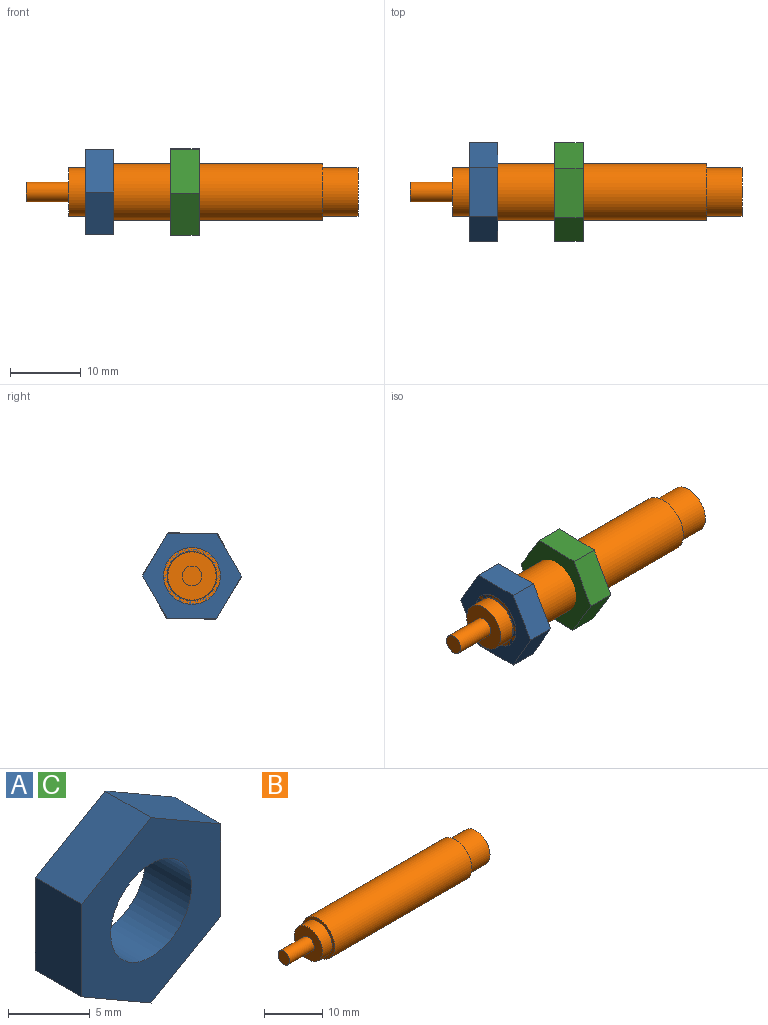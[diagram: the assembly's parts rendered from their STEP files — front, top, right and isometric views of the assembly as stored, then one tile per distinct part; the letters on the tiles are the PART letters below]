
ASSEMBLY  parts=3 mates=4
PART A: 9 faces, bbox 12x4x13.9 mm
  f0: plane 6.02x4mm, normal (0.5,0,0.87), area 27.8mm2, adj f1,f5,f6,f7
  f1: plane 6.02x4mm, normal (-0.5,0,0.87), area 27.8mm2, adj f0,f2,f6,f7
  f2: plane 6.95x4mm, normal (-1,0,0), area 27.8mm2, adj f1,f3,f6,f7
  f3: plane 6.02x4mm, normal (-0.5,0,-0.87), area 27.8mm2, adj f2,f4,f6,f7
  f4: plane 6.02x4mm, normal (0.5,0,-0.87), area 27.8mm2, adj f3,f5,f6,f7
  f5: plane 6.95x4mm, normal (1,0,0), area 27.8mm2, adj f0,f4,f6,f7
  f6: plane 13.9x12.04mm, normal (0,-1,0), area 87mm2, adj f0,f1,f2,f3,f4,f5,f8
  f7: plane 13.9x12.04mm, normal (0,1,0), area 87mm2, adj f0,f1,f2,f3,f4,f5,f8
  f8: cylinder r=3.5mm len=7mm, axis (0,-1,0), area 88mm2, adj f6,f7
PART B: 9 faces, bbox 46.8x8x8 mm
  f0: plane 2.8x2.8mm, normal (-1,0,0), area 6.2mm2, adj f8
  f1: plane 6.8x6.8mm, normal (1,0,0), area 36.3mm2, adj f2
  f2: cylinder r=3.4mm len=6.8mm, axis (1,0,0), area 106.8mm2, adj f1,f3
  f3: plane 8x8mm, normal (1,0,0), area 13.9mm2, adj f2,f4
  f4: cylinder r=4mm len=33.4mm, axis (1,0,0), area 839.4mm2, adj f3,f5
  f5: plane 8x8mm, normal (-1,0,0), area 13.9mm2, adj f4,f6
  f6: cylinder r=3.4mm len=6.8mm, axis (1,0,0), area 51.3mm2, adj f5,f7
  f7: plane 6.8x6.8mm, normal (-1,0,0), area 30.2mm2, adj f6,f8
  f8: cylinder r=1.4mm len=6mm, axis (1,0,0), area 52.8mm2, adj f0,f7
PART C: same geometry as A
PLACE A rot(axis=(0.58,0.58,-0.58),120deg) t=(-10.83,0,-0.14)mm
PLACE B t=(-23.23,0,-0.14)mm fixed
PLACE C rot(axis=(-0.69,-0.69,-0.19),157.9deg) t=(1.17,0,-0.14)mm
MATE cylindrical A.f8 <-> B.f2  axis (-1,0,0) through (-14.83,0,-0.14)mm
MATE planar A.f8 <-> B.f2  axis (-1,0,0) through (-14.83,0,-0.14)mm
MATE planar C.f8 <-> A.f8  axis (-1,0,0) through (-2.83,0,-0.14)mm
MATE cylindrical C.f8 <-> B.f2  axis (-1,0,0) through (-2.83,0,-0.14)mm
